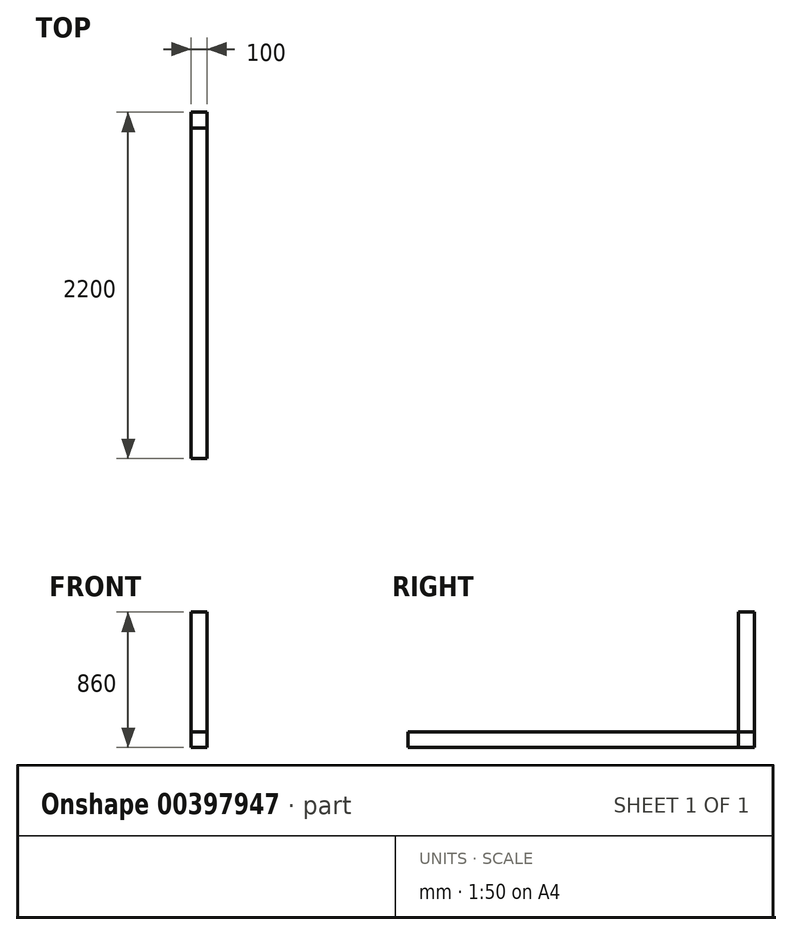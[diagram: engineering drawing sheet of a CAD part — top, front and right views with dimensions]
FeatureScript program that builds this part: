
annotation { "Feature Type Name" : "Feature", "Feature Type Description" : "" }
export const myFeature = defineFeature(function(context is Context, id is Id, definition is map)
    precondition{}
    {
        {
            var Q0;
            Q0=qCreatedBy(makeId("Front.planeOp"),FACE);
            var sketch = newSketch(context, id + "F0", { "sketchPlane" : qUnion([Q0])});
            skLineSegment(sketch, "E0.bottom", {"start": v(-1100, 480) * mm, "end": v(1100, 480) * mm});
            skLineSegment(sketch, "E0.top", {"start": v(-1100, -480) * mm, "end": v(1100, -480) * mm});
            skLineSegment(sketch, "E0.left", {"start": v(-1100, 480) * mm, "end": v(-1100, -480) * mm});
            skLineSegment(sketch, "E0.right", {"start": v(1100, 480) * mm, "end": v(1100, -480) * mm});
            skPoint(sketch, "E0.middle", {"position": v(0, 0) * mm});
            skLineSegment(sketch, "E1.bottom", {"start": v(-50, -380) * mm, "end": v(50, -380) * mm});
            skLineSegment(sketch, "E1.top", {"start": v(-50, -480) * mm, "end": v(50, -480) * mm});
            skLineSegment(sketch, "E1.left", {"start": v(-50, -380) * mm, "end": v(-50, -480) * mm});
            skLineSegment(sketch, "E1.right", {"start": v(50, -380) * mm, "end": v(50, -480) * mm});
            skLineSegment(sketch, "E2.bottom", {"start": v(-1100, 480) * mm, "end": v(-1000, 480) * mm});
            skLineSegment(sketch, "E2.top", {"start": v(-1100, 380) * mm, "end": v(-1000, 380) * mm});
            skLineSegment(sketch, "E2.left", {"start": v(-1100, 480) * mm, "end": v(-1100, 380) * mm});
            skLineSegment(sketch, "E2.right", {"start": v(-1000, 480) * mm, "end": v(-1000, 380) * mm});
            skLineSegment(sketch, "E3", {"start": v(-1000, 380) * mm, "end": v(-50, -380) * mm});
            skLineSegment(sketch, "E4.bottom", {"start": v(1100, 480) * mm, "end": v(1000, 480) * mm});
            skLineSegment(sketch, "E4.top", {"start": v(1100, 380) * mm, "end": v(1000, 380) * mm});
            skLineSegment(sketch, "E4.left", {"start": v(1100, 480) * mm, "end": v(1100, 380) * mm});
            skLineSegment(sketch, "E4.right", {"start": v(1000, 480) * mm, "end": v(1000, 380) * mm});
            skLineSegment(sketch, "E5", {"start": v(-1100, 380) * mm, "end": v(-50, -480) * mm});
            skLineSegment(sketch, "E6.bottom", {"start": v(-50, 480) * mm, "end": v(50, 480) * mm});
            skLineSegment(sketch, "E6.top", {"start": v(-50, 380) * mm, "end": v(50, 380) * mm});
            skLineSegment(sketch, "E6.left", {"start": v(-50, 480) * mm, "end": v(-50, 380) * mm});
            skLineSegment(sketch, "E6.right", {"start": v(50, 480) * mm, "end": v(50, 380) * mm});
            skLineSegment(sketch, "E7", {"start": v(-50, 380) * mm, "end": v(-50, -380) * mm});
            skLineSegment(sketch, "E8", {"start": v(50, 380) * mm, "end": v(50, -380) * mm});
            skLineSegment(sketch, "E9", {"start": v(50, -480) * mm, "end": v(1100, 380) * mm});
            skLineSegment(sketch, "E10", {"start": v(1000, 380) * mm, "end": v(50, -380) * mm});
            skSolve(sketch);
        }
        {
            var Q0;
            Q0=makeQuery(id+"F0.imprint","IMPRINT",FACE,{"disambiguationData":[TD([[makeQuery(id+"F0.imprint","IMPRINT",EDGE,{"derivedFrom":sQuery(id+"F0.wireOp",EDGE,"E6.bottom")}),-1.0]])]});
            var Q1;
            Q1=makeQuery(id+"F0.imprint","IMPRINT",FACE,{"disambiguationData":[TD([[makeQuery(id+"F0.imprint","IMPRINT",EDGE,{"derivedFrom":sQuery(id+"F0.wireOp",EDGE,"E4.bottom")}),1.0]])]});
            var Q2;
            Q2=makeQuery(id+"F0.imprint","IMPRINT",FACE,{"disambiguationData":[TD([[makeQuery(id+"F0.imprint","IMPRINT",EDGE,{"derivedFrom":sQuery(id+"F0.wireOp",EDGE,"E1.bottom")}),-1.0]])]});
            var Q3;
            Q3=makeQuery(id+"F0.imprint","IMPRINT",FACE,{"disambiguationData":[TD([[makeQuery(id+"F0.imprint","IMPRINT",EDGE,{"derivedFrom":sQuery(id+"F0.wireOp",EDGE,"E2.bottom")}),-1.0]])]});
            extrude(context, id + "F1", {"entities" : qUnion([Q0, Q1, Q2, Q3]), "depth" : 2200 * mm});
        }
        {
            var Q0;
            Q0=makeQuery(id+"F0.imprint","IMPRINT",FACE,{"disambiguationData":[TD([[makeQuery(id+"F0.imprint","IMPRINT",EDGE,{"derivedFrom":sQuery(id+"F0.wireOp",EDGE,"E1.bottom")}),-1.0]])]});
            var Q1;
            Q1=makeQuery(id+"F0.imprint","IMPRINT",FACE,{"disambiguationData":[TD([[makeQuery(id+"F0.imprint","IMPRINT",EDGE,{"derivedFrom":sQuery(id+"F0.wireOp",EDGE,"E2.bottom")}),-1.0]])]});
            var Q2;
            Q2=makeQuery(id+"F0.imprint","IMPRINT",FACE,{"disambiguationData":[TD([[makeQuery(id+"F0.imprint","IMPRINT",EDGE,{"derivedFrom":sQuery(id+"F0.wireOp",EDGE,"E6.bottom")}),-1.0]])]});
            var Q3;
            Q3=makeQuery(id+"F0.imprint","IMPRINT",FACE,{"disambiguationData":[TD([[makeQuery(id+"F0.imprint","IMPRINT",EDGE,{"derivedFrom":sQuery(id+"F0.wireOp",EDGE,"E4.bottom")}),1.0]])]});
            var Q4;
            Q4=makeQuery(id+"F0.imprint","IMPRINT",FACE,{"disambiguationData":[TD([[makeQuery(id+"F0.imprint","IMPRINT",EDGE,{"derivedFrom":sQuery(id+"F0.wireOp",EDGE,"E1.bottom")}),1.0]])]});
            extrude(context, id + "F2", {"entities" : qUnion([Q0, Q1, Q2, Q3, Q4]), "depth" : 100 * mm});
        }
    });
